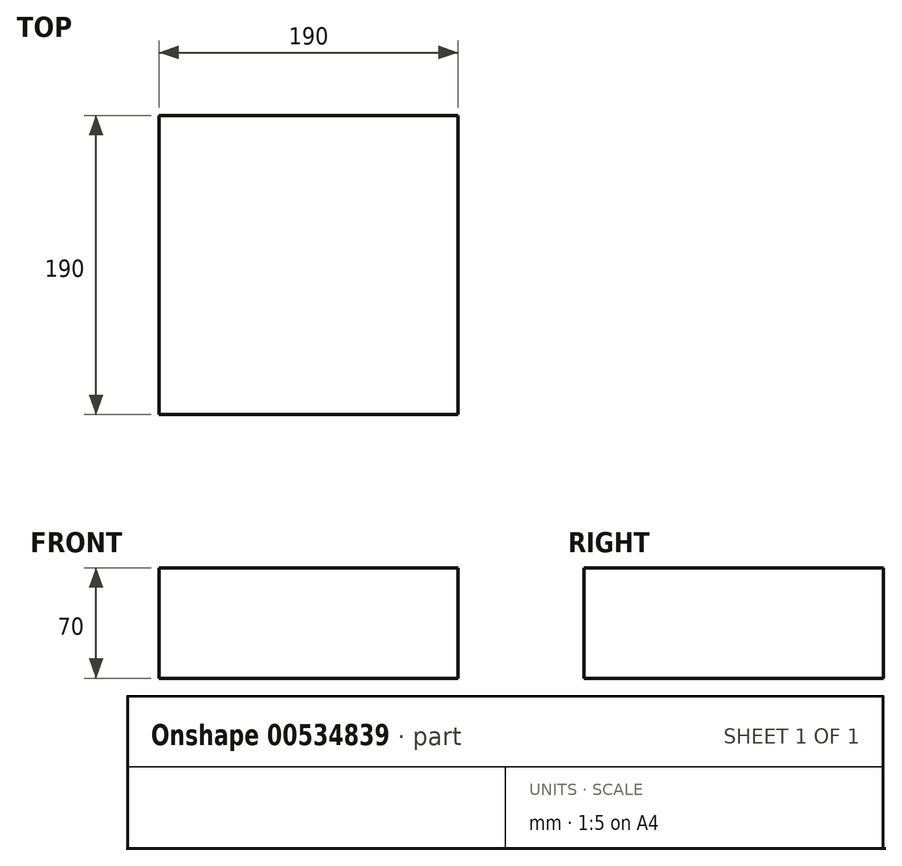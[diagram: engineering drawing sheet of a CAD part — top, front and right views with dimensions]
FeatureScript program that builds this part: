
annotation { "Feature Type Name" : "Feature", "Feature Type Description" : "" }
export const myFeature = defineFeature(function(context is Context, id is Id, definition is map)
    precondition{}
    {
        {
            var Q0;
            Q0=qCreatedBy(makeId("Top.planeOp"),FACE);
            var sketch = newSketch(context, id + "F0", { "sketchPlane" : qUnion([Q0])});
            skLineSegment(sketch, "E0.bottom", {"start": v(95, -95) * mm, "end": v(-95, -95) * mm});
            skLineSegment(sketch, "E0.top", {"start": v(95, 95) * mm, "end": v(-95, 95) * mm});
            skLineSegment(sketch, "E0.left", {"start": v(95, -95) * mm, "end": v(95, 95) * mm});
            skLineSegment(sketch, "E0.right", {"start": v(-95, -95) * mm, "end": v(-95, 95) * mm});
            skPoint(sketch, "E0.middle", {"position": v(0, 0) * mm});
            skSolve(sketch);
        }
        {
            var Q0;
            Q0=makeQuery(id+"F0.imprint","IMPRINT",FACE,{"disambiguationData":[TD([[makeQuery(id+"F0.imprint","IMPRINT",EDGE,{"derivedFrom":sQuery(id+"F0.wireOp",EDGE,"E0.bottom")}),-1.0]])]});
            extrude(context, id + "F1", {"entities" : qUnion([Q0]), "depth" : 70 * mm, "offsetDistance" : 25 * mm});
        }
    });
